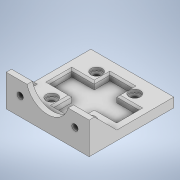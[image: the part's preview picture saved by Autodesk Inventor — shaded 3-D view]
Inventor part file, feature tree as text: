
AUTODESK INVENTOR PART (.ipt)
format: ipt  version: 2020 (Build 240168000, 168)  size: 256,000 bytes
history: native  units: in
note: dims shown in document units (in); Inventor stores cm internally (conversion verified against a paired STEP export)
features: extrude x8, sketch x8, chamfer x3
ambient origin geometry x8: Origin, YZ Plane, XZ Plane, XY Plane, X Axis, Y Axis, Z Axis, Center Point
bodies: Solid1 (feature_tree)
feature tree (19):
  extrude  "Extrusion1"  Depth=0.5in
  extrude  "Extrusion2"  Depth=0.208in TaperAngle=0.0deg
  extrude  "Extrusion3"  Depth=0.0787in
  chamfer  "Chamfer1"  Distance=0.5in
  extrude  "Extrusion4"  Depth=0.125in
  extrude  "Extrusion5"  Depth=0.236in
  extrude  "Extrusion6"  Depth=0.125in
  extrude  "Extrusion7"  Depth=0.125in
  chamfer  "Chamfer2"  Distance=0.2in
  extrude  "Extrusion8"  Depth=0.5in TaperAngle=0.0deg
  chamfer  "Chamfer3"  Distance=1.8898in
  sketch  "Sketch1"  dims[d0=1.8504in d1=0.5in]
  sketch  "Sketch2"  dims[d2=0.1181in d3=0.0in d4=0.208in d5=0.0in]
  sketch  "Sketch3"  dims[d6=0.0in d7=0.0787in]
  sketch  "Sketch4"  dims[d8=0.0787in]
  sketch  "Sketch5"  dims[d9=0.5in d10=0.5in d11=0.0in]
  sketch  "Sketch6"  dims[d12=0.5in d13=0.125in d14=45.0deg d15=0.1378in]
  sketch  "Sketch7"  dims[d16=0.1378in d17=0.236in]
  sketch  "Sketch8"  dims[d18=1.2205in d19=0.2364in d20=0.2in d21=0.2in d22=0.5in d23=0.0in d24=1.8898in d25=0.0in d26=0.9449in d27=0.9252in d28=0.8268in d29=0.208in d30=0.0in d31=0.125in d32=0.125in d33=0.125in d34=0.125in d35=0.4in d36=1.0in d37=1.0in d38=0.4in d39=0.5in d40=0.5in d41=0.5in d42=0.5in d43=0.208in d44=0.0in d45=0.25in d46=0.25in d47=0.25in d48=0.25in d49=0.058in d50=0.0in d51=0.04in d52=0.125in d53=45.0deg d54=0.5in d55=1.5in d56=0.175in d57=0.1754in d58=0.6in d59=0.5in d60=0.675in d61=0.6754in d62=1.25in d63=0.25in d64=0.15in d65=0.0in d66=0.04in d67=0.125in d68=45.0deg]
